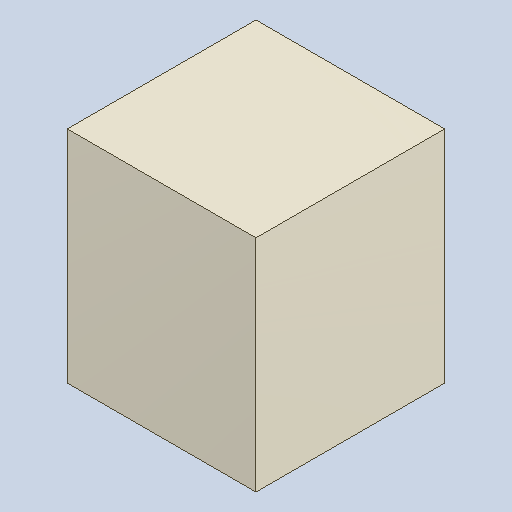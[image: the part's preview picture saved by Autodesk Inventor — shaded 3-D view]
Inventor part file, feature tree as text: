
AUTODESK INVENTOR PART (.ipt)
format: ipt  version: 2023.4 (Build 274418000, 418)  size: 82,944 bytes
history: native  units: mm
features: extrude x1
ambient origin geometry x8: Origin, YZ Plane, XZ Plane, XY Plane, X Axis, Y Axis, Z Axis, Center Point
bodies: Solid1 (feature_tree)
feature tree (1):
  extrude  "Extruded_21"  [1 undecoded]
note: 1 required parameter value undecoded (feature->parameter linkage not recoverable at this tier; creation-order binding heuristic only, values carry confidence <= 0.55)
